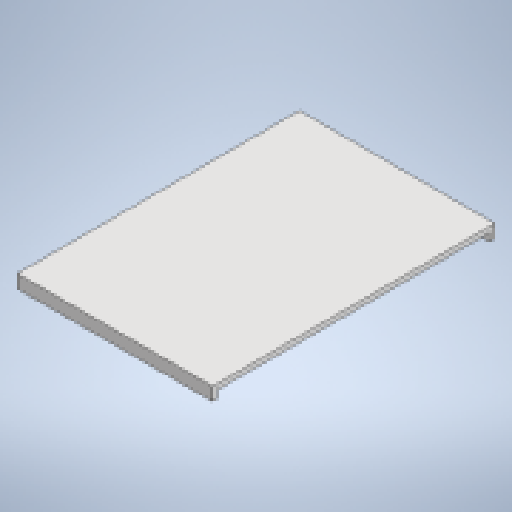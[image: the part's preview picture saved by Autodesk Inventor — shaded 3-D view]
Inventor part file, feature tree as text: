
AUTODESK INVENTOR PART (.ipt)
format: ipt  version: 2024 (Build 280153000, 153)  size: 220,160 bytes
history: native  units: mm
features: extrude x2, sketch x2
ambient origin geometry x8: Origin, YZ Plane, XZ Plane, XY Plane, X Axis, Y Axis, Z Axis, Center Point
bodies: Solid1 (feature_tree)
feature tree (4):
  extrude  "Extrusion1"  Depth=180.0mm
  extrude  "Extrusion2"  Depth=5.0mm
  sketch  "Sketch1"  dims[d0=260.0mm d1=180.0mm]
  sketch  "Sketch2"  dims[d2=5.0mm d3=0.0mm d4=5.0mm d5=5.0mm d6=7.0mm d7=0.0mm]
